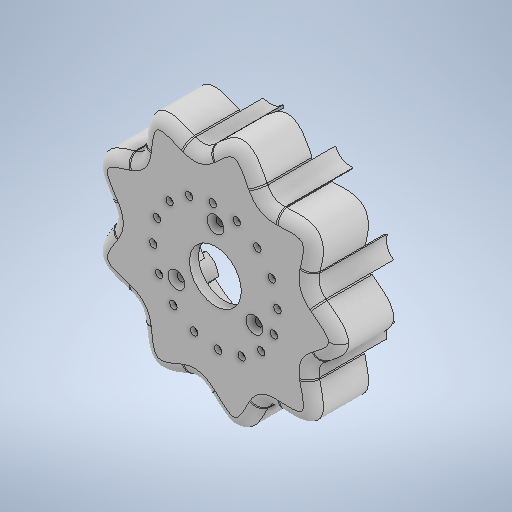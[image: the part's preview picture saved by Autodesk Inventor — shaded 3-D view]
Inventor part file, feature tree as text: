
AUTODESK INVENTOR PART (.ipt)
format: ipt  version: 2025 (Build 290162000, 162)  size: 1,079,808 bytes
history: native  units: mm
features: sketch x8, extrude x6, chamfer x1, fillet x1, other x1
ambient origin geometry x8: Origin, YZ Plane, XZ Plane, XY Plane, X Axis, Y Axis, Z Axis, Center Point
bodies: 实体1 (feature_tree)
feature tree (17):
  sketch  "草图1"  dims[d0=67.5mm d1=40.0mm]
  extrude  "拉伸1"  Depth=40.0mm
  extrude  "拉伸2"  Depth=30.0mm TaperAngle=360.0deg
  sketch  "草图2"  dims[d7=1.0mm d8=0.0mm d9=3600.0mm]
  extrude  "拉伸5"  Depth=3600.0mm TaperAngle=0.0deg
  extrude  "拉伸6"  Depth=4.0mm TaperAngle=0.0deg
  sketch  "草图4"  dims[d21=67.0mm]
  extrude  "拉伸7"  Depth=2.0mm TaperAngle=45.0deg
  chamfer  "倒角1"  Distance=96.0mm
  extrude  "拉伸8"  Depth=85.1mm
  fillet  "圆角2"  Radius=1.0mm
  sketch  "草图 - 环形阵列1"  dims[d2=3.4mm d3=30.0mm d5=360.0deg]
  other  "二维表达式曲线1"
  sketch  "草图 - 环形阵列2"  dims[d10=23.0mm d11=4.0mm d12=0.0mm]
  sketch  "草图3"  dims[d13=20.0mm d14=0.0mm d15=2.0mm d16=2.0mm d17=45.0deg]
  sketch  "草图 - 环形阵列3"  dims[d20=84.5mm]
  sketch  "草图 - 环形阵列5"  dims[d22=90.0mm d23=96.0mm d24=85.1mm d25=1.0mm d28=1.0mm d31=0.5mm d37=90.0mm d39=360.0deg d41=30.0mm d42=0.0mm d43=3.15mm d44=90.0mm d46=360.0deg d48=8.0mm d49=0.0mm d50=55.25mm d51=10.15mm d56=2.0mm d57=0.0mm d58=3.3mm d59=160.0mm d61=360.0deg d63=10.0mm d64=0.0mm d65=5.0mm]
